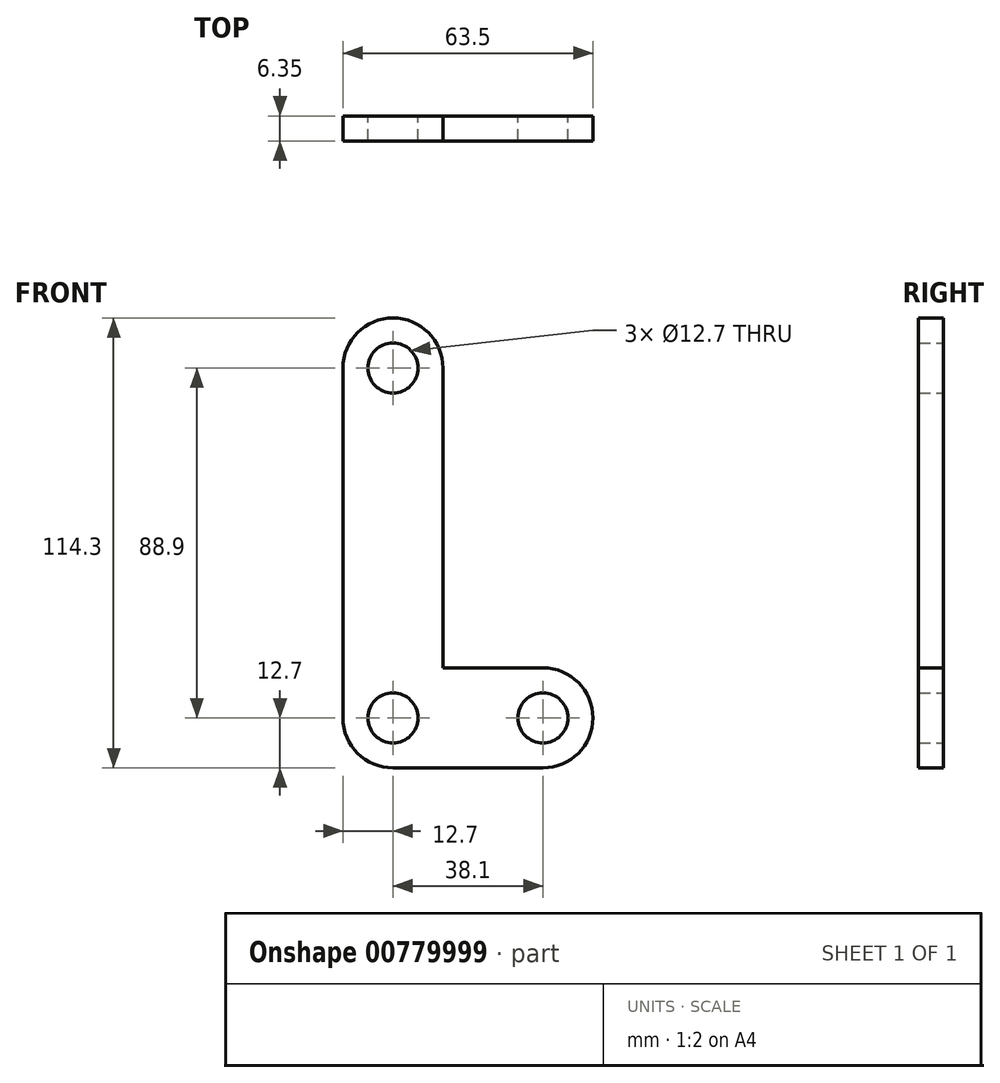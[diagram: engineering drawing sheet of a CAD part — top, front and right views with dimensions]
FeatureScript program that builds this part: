
annotation { "Feature Type Name" : "Feature", "Feature Type Description" : "" }
export const myFeature = defineFeature(function(context is Context, id is Id, definition is map)
    precondition{}
    {
        {
            var Q0;
            Q0=qCreatedBy(makeId("Front.planeOp"),FACE);
            var sketch = newSketch(context, id + "F0", { "sketchPlane" : qUnion([Q0])});
            skLineSegment(sketch, "E0", {"start": v(0, 12.7) * mm, "end": v(0, 101.6) * mm});
            skLineSegment(sketch, "E1", {"start": v(25.4, 101.6) * mm, "end": v(25.4, 25.4) * mm});
            skLineSegment(sketch, "E2", {"start": v(25.4, 25.4) * mm, "end": v(50.8, 25.4) * mm});
            skLineSegment(sketch, "E3", {"start": v(50.8, 0) * mm, "end": v(12.7, 0) * mm});
            skArc(sketch, "E4", {"start": v(25.4, 101.6) * mm, "mid": v(12.7, 114.3) * mm, "end": v(0, 101.6) * mm});
            skArc(sketch, "E5", {"start": v(50.8, 0) * mm, "mid": v(63.5, 12.7) * mm, "end": v(50.8, 25.4) * mm});
            skCircle(sketch, "E6", {"center": v(12.7, 101.6) * mm, "radius": 6.35 * mm});
            skCircle(sketch, "E7", {"center": v(50.8, 12.7) * mm, "radius": 6.35 * mm});
            skCircle(sketch, "E8", {"center": v(12.7, 12.7) * mm, "radius": 6.35 * mm});
            skArc(sketch, "E9", {"start": v(0, 12.7) * mm, "mid": v(3.72, 3.72) * mm, "end": v(12.7, 0) * mm});
            skPoint(sketch, "E10.orphan", {"position": v(0, 0) * mm});
            skSolve(sketch);
        }
        {
            var Q0;
            Q0 = qSketchRegion(id + "F0", true);
            extrude(context, id + "F1", {"entities" : qUnion([Q0]), "depth" : 6.35 * mm, "offsetDistance" : 25.4 * mm});
        }
    });
